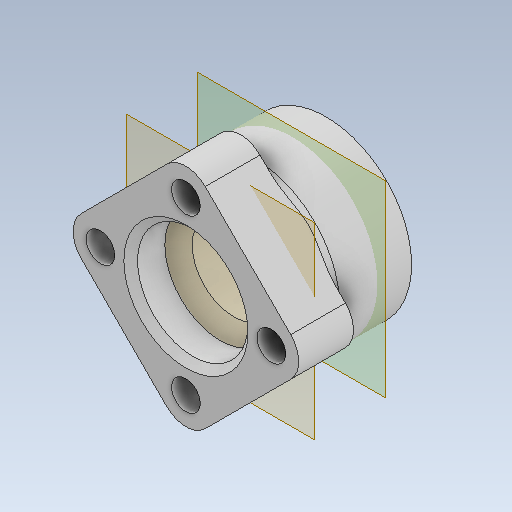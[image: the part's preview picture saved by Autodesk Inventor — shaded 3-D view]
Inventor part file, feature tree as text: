
AUTODESK INVENTOR PART (.ipt)
format: ipt  version: 2020 (Build 240168000, 168)  size: 251,904 bytes
history: native  units: mm
features: sketch x5, extrude x5, plane x3, pattern_circular x3, projected_geometry x3, other x3, chamfer x2, fillet x1, reference x1
ambient origin geometry x8: Origin, YZ Plane, XZ Plane, XY Plane, X Axis, Y Axis, Z Axis, Center Point
bodies: Solid1 (feature_tree)
feature tree (26):
  sketch  "Sketch1"  dims[d0=16.15mm d1=25.0mm]
  plane  "Work Plane1"
  extrude  "Extrusion1"  Depth=25.0mm
  plane  "Work Plane2"
  plane  "Work Plane3"
  extrude  "Extrusion2"  [1 undecoded]
  chamfer  "Chamfer1"  Distance=10.0mm
  extrude  "Extrusion3"  Depth=8.0mm
  pattern_circular  "Circular Pattern1"  [2 undecoded]
  extrude  "Extrusion5"  Depth=2.0mm TaperAngle=360.0deg
  pattern_circular  "Circular Pattern3"  [2 undecoded]
  extrude  "Extrusion6"  Depth=2.0mm TaperAngle=360.0deg
  pattern_circular  "Circular Pattern4"  [2 undecoded]
  fillet  "Fillet1"  Radius=6.0mm
  chamfer  "Chamfer2"  Distance=40.0mm Angle=360.0deg
  reference  "Reference1"
  sketch  "Sketch2"  dims[d2=10.0mm d3=0.0mm d4=-5.0mm]
  sketch  "Sketch3"  dims[d5=-5.0mm]
  projected_geometry  "Projected Loop1"
  sketch  "Sketch6"  dims[d6=2.0mm d7=10.0mm d8=0.0mm]
  projected_geometry  "Projected Loop4"
  sketch  "Sketch7"  dims[d9=2.0mm d10=2.0mm d11=45.0deg d12=8.0mm d13=8.0mm d14=0.0mm d15=40.0mm d16=360.0deg d24=8.0mm d25=0.0mm d26=40.0mm d27=360.0deg d29=4.2mm d30=6.0mm d31=0.0mm d32=40.0mm d33=360.0deg d35=2.0mm d36=1.0mm d37=2.0mm d38=45.0deg]
  projected_geometry  "Projected Loop5"
  parser-record x1  (decoder bookkeeping rows leaked as tree rows — omitted from the tree; the rows remain in map.json)
  other  "reducer_2.iam"
  other  "xl_60_out_2:1"
note: 7 required parameter values undecoded (feature->parameter linkage not recoverable at this tier; creation-order binding heuristic only, values carry confidence <= 0.55)
note: 1 file-system path scrubbed to <path> (originals preserved in map.json)
